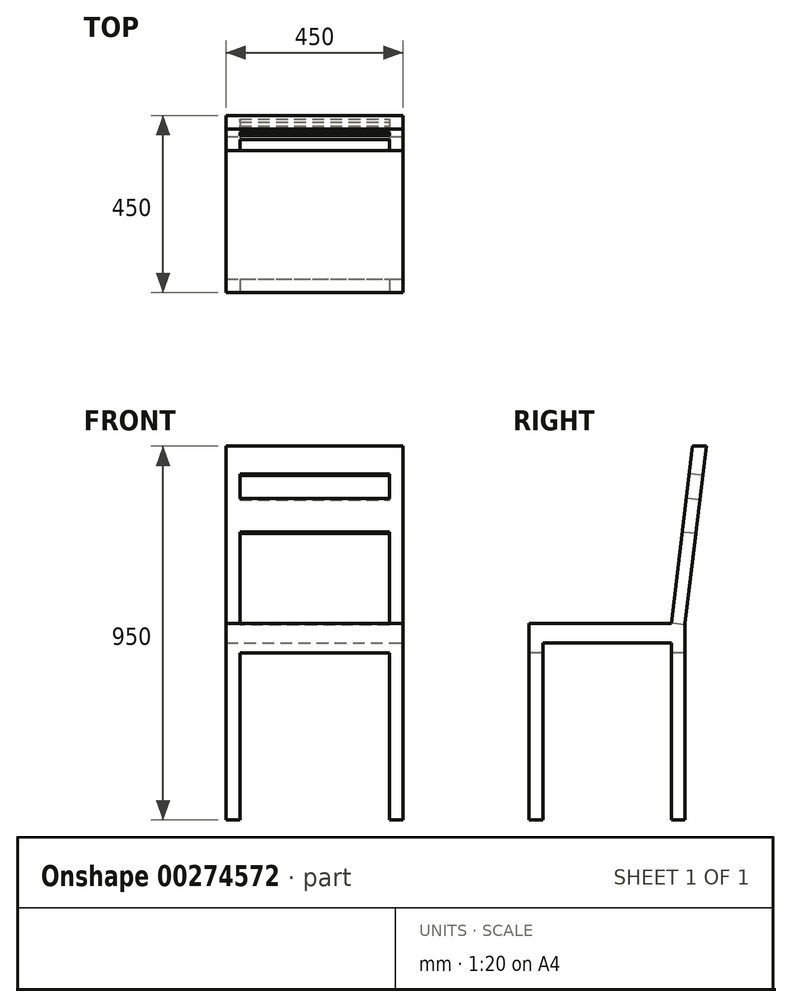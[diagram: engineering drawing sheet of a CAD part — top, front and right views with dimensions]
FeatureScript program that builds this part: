
annotation { "Feature Type Name" : "Feature", "Feature Type Description" : "" }
export const myFeature = defineFeature(function(context is Context, id is Id, definition is map)
    precondition{}
    {
        {
            var Q0;
            Q0=qCreatedBy(makeId("Top.planeOp"),FACE);
            var sketch = newSketch(context, id + "F0", { "sketchPlane" : qUnion([Q0])});
            skLineSegment(sketch, "E0.bottom", {"start": v(225, 225) * mm, "end": v(-225, 225) * mm});
            skLineSegment(sketch, "E0.top", {"start": v(225, -225) * mm, "end": v(-225, -225) * mm});
            skLineSegment(sketch, "E0.left", {"start": v(225, 225) * mm, "end": v(225, -225) * mm});
            skLineSegment(sketch, "E0.right", {"start": v(-225, 225) * mm, "end": v(-225, -225) * mm});
            skPoint(sketch, "E0.middle", {"position": v(0, 0) * mm});
            skSolve(sketch);
        }
        {
            var Q0;
            Q0=qSketchRegion(id+"F0",true);
            extrude(context, id + "F1", {"entities" : qUnion([Q0]), "depth" : 950 * mm});
        }
        {
            var Q0;
            Q0=makeQuery(id+"F1.opExtrude","SWEPT_FACE",FACE,{"disambiguationData":[OSD([sQuery(id+"F0.wireOp",EDGE,"E0.left")])]});
            var sketch = newSketch(context, id + "F2", { "sketchPlane" : qUnion([Q0])});
            skLineSegment(sketch, "E1.left", {"start": v(-225, 500) * mm, "end": v(-225, 450) * mm});
            skLineSegment(sketch, "E2", {"start": v(136.41, 450) * mm, "end": v(136.41, 0) * mm});
            skLineSegment(sketch, "E3", {"start": v(136.41, 0) * mm, "end": v(171.41, 0) * mm});
            skLineSegment(sketch, "E4", {"start": v(-225, 500) * mm, "end": v(225, 500) * mm});
            skLineSegment(sketch, "E5", {"start": v(-225, 450) * mm, "end": v(225, 450) * mm});
            skLineSegment(sketch, "E6", {"start": v(225, 950) * mm, "end": v(171.41, 500) * mm});
            skLineSegment(sketch, "E7", {"start": v(136.41, 500) * mm, "end": v(190, 950) * mm});
            skLineSegment(sketch, "E8", {"start": v(171.41, 0) * mm, "end": v(171.41, 500) * mm});
            skLineSegment(sketch, "E9", {"start": v(136.41, 500) * mm, "end": v(136.41, 450) * mm});
            skLineSegment(sketch, "E10", {"start": v(-190, 450) * mm, "end": v(-190, 0) * mm});
            skSolve(sketch);
        }
        {
            var Q0;
            {var subQ4=sQuery(id+"F2.wireOp",EDGE,"E7");Q0=makeQuery(id+"F2.imprint","IMPRINT",FACE,{"disambiguationData":[TD([[makeQuery(id+"F2.imprint","IMPRINT",EDGE,{"derivedFrom":subQ4}),1.0]])]});}
            var Q1;
            {var subQ4=sQuery(id+"F2.wireOp",EDGE,"E6");Q1=makeQuery(id+"F2.imprint","IMPRINT",FACE,{"disambiguationData":[TD([[makeQuery(id+"F2.imprint","IMPRINT",EDGE,{"derivedFrom":subQ4}),1.0]])]});}
            var Q2;
            {var subQ3=sQuery(id+"F2.wireOp",EDGE,"E8");var subQ5=sQuery(id+"F2.wireOp",EDGE,"E5");var subQ6=makeQuery(id+"F2.imprint","INTERSECT",VERTEX,{"derivedFrom":[subQ5,subQ3]});Q2=makeQuery(id+"F2.imprint","IMPRINT",FACE,{"disambiguationData":[TD([[makeQuery(id+"F2.imprint","IMPRINT",EDGE,{"disambiguationData":[TD([[subQ6,-1.0]])],"derivedFrom":subQ5}),1.0]])]});}
            var Q3;
            {var subQ0=sQuery(id+"F2.wireOp",EDGE,"E5");var subQ4=sQuery(id+"F2.wireOp",EDGE,"E8");var subQ5=makeQuery(id+"F2.imprint","INTERSECT",VERTEX,{"derivedFrom":[subQ0,subQ4]});Q3=makeQuery(id+"F2.imprint","IMPRINT",FACE,{"disambiguationData":[TD([[makeQuery(id+"F2.imprint","IMPRINT",EDGE,{"disambiguationData":[TD([[subQ5,-1.0]])],"derivedFrom":subQ0}),-1.0]])]});}
            var Q4;
            {var subQ0=sQuery(id+"F2.wireOp",EDGE,"E2");Q4=makeQuery(id+"F2.imprint","IMPRINT",FACE,{"disambiguationData":[TD([[makeQuery(id+"F2.imprint","IMPRINT",EDGE,{"derivedFrom":subQ0}),-1.0]])]});}
            extrude(context, id + "F3", {"entities" : qUnion([Q0, Q1, Q2, Q3, Q4]), "operationType" : NewBodyOperationType.REMOVE, "endBound" : BoundingType.THROUGH_ALL, "oppositeDirection" : true, "depth" : 25 * mm});
        }
        {
            var Q0;
            Q0=makeQuery(id+"F1.opExtrude","SWEPT_FACE",FACE,{"disambiguationData":[OSD([sQuery(id+"F0.wireOp",EDGE,"E0.top")])]});
            var sketch = newSketch(context, id + "F4", { "sketchPlane" : qUnion([Q0])});
            skLineSegment(sketch, "E11", {"start": v(-190, 0) * mm, "end": v(-190, 425) * mm});
            skLineSegment(sketch, "E12", {"start": v(-190, 425) * mm, "end": v(190, 425) * mm});
            skLineSegment(sketch, "E13", {"start": v(190, 425) * mm, "end": v(190, 0) * mm});
            skSolve(sketch);
        }
        {
            var Q0;
            Q0 = qSketchRegion(id + "F4", true);
            var Q1;
            {var subQ0=sQuery(id+"F4.wireOp",EDGE,"E11");Q1=makeQuery(id+"F4.imprint","IMPRINT",FACE,{"disambiguationData":[TD([[makeQuery(id+"F4.imprint","IMPRINT",EDGE,{"derivedFrom":subQ0}),-1.0]])]});}
            extrude(context, id + "F5", {"entities" : qUnion([Q0, Q1]), "operationType" : NewBodyOperationType.REMOVE, "endBound" : BoundingType.THROUGH_ALL, "oppositeDirection" : true, "depth" : 25 * mm});
        }
        {
            var Q0;
            Q0=makeQuery(id+"F3.boolean.opBoolean","COPY",FACE,{"derivedFrom":makeQuery(id+"F3.opExtrude","SWEPT_FACE",FACE,{"disambiguationData":[OSD([sQuery(id+"F2.wireOp",EDGE,"E7")])]})});
            var sketch = newSketch(context, id + "F6", { "sketchPlane" : qUnion([Q0])});
            skLineSegment(sketch, "E14", {"start": v(-190, 512.62) * mm, "end": v(-190, 894.94) * mm});
            skLineSegment(sketch, "E15", {"start": v(-190, 894.94) * mm, "end": v(190, 894.94) * mm});
            skLineSegment(sketch, "E16", {"start": v(190, 894.94) * mm, "end": v(190, 512.62) * mm});
            skLineSegment(sketch, "E17", {"start": v(-190, 832.1) * mm, "end": v(190, 832.1) * mm});
            skLineSegment(sketch, "E18", {"start": v(-190, 745.94) * mm, "end": v(190, 745.94) * mm});
            skSolve(sketch);
        }
        {
            var Q0;
            {var subQ3=sQuery(id+"F6.wireOp",EDGE,"E18");Q0=makeQuery(id+"F6.imprint","IMPRINT",FACE,{"disambiguationData":[TD([[makeQuery(id+"F6.imprint","IMPRINT",EDGE,{"derivedFrom":subQ3}),-1.0]])]});}
            var Q1;
            {var subQ0=sQuery(id+"F6.wireOp",EDGE,"E15");Q1=makeQuery(id+"F6.imprint","IMPRINT",FACE,{"disambiguationData":[TD([[makeQuery(id+"F6.imprint","IMPRINT",EDGE,{"derivedFrom":subQ0}),-1.0]])]});}
            extrude(context, id + "F7", {"entities" : qUnion([Q0, Q1]), "operationType" : NewBodyOperationType.REMOVE, "endBound" : BoundingType.THROUGH_ALL, "oppositeDirection" : true, "depth" : 25 * mm});
        }
    });
